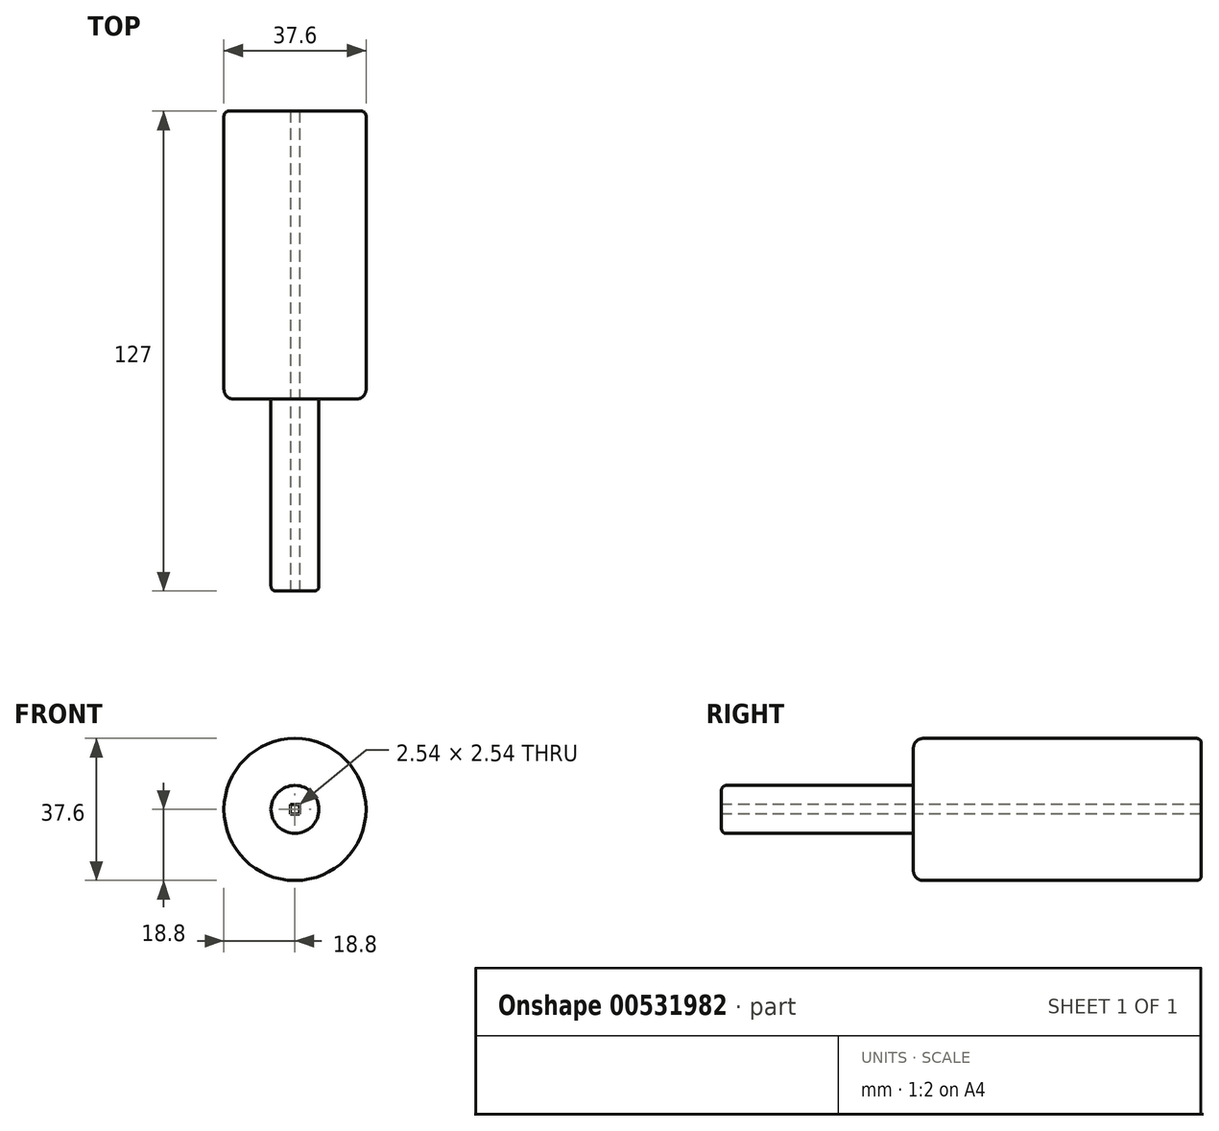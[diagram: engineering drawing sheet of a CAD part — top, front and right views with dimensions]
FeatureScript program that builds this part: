
annotation { "Feature Type Name" : "Feature", "Feature Type Description" : "" }
export const myFeature = defineFeature(function(context is Context, id is Id, definition is map)
    precondition{}
    {
        {
            var Q0;
            Q0=qCreatedBy(makeId("Front.planeOp"),FACE);
            var sketch = newSketch(context, id + "F0", { "sketchPlane" : qUnion([Q0])});
            skCircle(sketch, "E0", {"center": v(0, 0) * mm, "radius": 18.8 * mm});
            skSolve(sketch);
        }
        {
            var Q0;
            Q0=makeQuery(id+"F0.imprint","IMPRINT",FACE,{"disambiguationData":[TD([[makeQuery(id+"F0.imprint","IMPRINT",EDGE,{"derivedFrom":sQuery(id+"F0.wireOp",EDGE,"E0")}),1.0]])]});
            var sketch = newSketch(context, id + "F1", { "sketchPlane" : qUnion([Q0])});
            skCircle(sketch, "E1", {"center": v(0, 0) * mm, "radius": 6.35 * mm});
            skSolve(sketch);
        }
        {
            var Q0;
            Q0 = qSketchRegion(id + "F0", true);
            extrude(context, id + "F2", {"entities" : qUnion([Q0]), "depth" : 76.2 * mm, "offsetDistance" : 25.4 * mm});
        }
        {
            var Q0;
            Q0=makeQuery(id+"F1.imprint","IMPRINT",FACE,{"disambiguationData":[TD([[makeQuery(id+"F1.imprint","IMPRINT",EDGE,{"derivedFrom":sQuery(id+"F1.wireOp",EDGE,"E1")}),1.0]])]});
            extrude(context, id + "F3", {"entities" : qUnion([Q0]), "operationType" : NewBodyOperationType.ADD, "depth" : 127 * mm, "offsetDistance" : 25.4 * mm});
        }
        {
            var Q0;
            Q0=makeQuery(id+"F2.opExtrude","CAP_EDGE",EDGE,{"disambiguationData":[OSD([sQuery(id+"F0.wireOp",EDGE,"E0")])],"isStart":true});
            var Q1;
            Q1=makeQuery(id+"F3.opExtrude","CAP_EDGE",EDGE,{"disambiguationData":[OSD([sQuery(id+"F1.wireOp",EDGE,"E1")])],"isStart":false});
            fillet(context, id + "F4", {"entities" : qUnion([Q0, Q1]), "radius" : 1.27 * mm, "tangentPropagation" : true, "allowEdgeOverflow" : false});
        }
        {
            var Q0;
            Q0=makeQuery(id+"F3.opExtrude","CAP_FACE",FACE,{"disambiguationData":[OSD([sQuery(id+"F1.wireOp",EDGE,"E1")])],"isStart":false});
            var sketch = newSketch(context, id + "F5", { "sketchPlane" : qUnion([Q0])});
            skLineSegment(sketch, "E2.bottom", {"start": v(1.27, 1.27) * mm, "end": v(-1.27, 1.27) * mm});
            skLineSegment(sketch, "E2.top", {"start": v(1.27, -1.27) * mm, "end": v(-1.27, -1.27) * mm});
            skLineSegment(sketch, "E2.left", {"start": v(1.27, 1.27) * mm, "end": v(1.27, -1.27) * mm});
            skLineSegment(sketch, "E2.right", {"start": v(-1.27, 1.27) * mm, "end": v(-1.27, -1.27) * mm});
            skPoint(sketch, "E2.middle", {"position": v(0, 0) * mm});
            skSolve(sketch);
        }
        {
            var Q0;
            Q0 = qSketchRegion(id + "F5", true);
            extrude(context, id + "F6", {"entities" : qUnion([Q0]), "operationType" : NewBodyOperationType.REMOVE, "oppositeDirection" : true, "depth" : 127 * mm, "offsetDistance" : 25.4 * mm});
        }
        {
            var Q0;
            Q0=makeQuery(id+"F2.opExtrude","CAP_EDGE",EDGE,{"disambiguationData":[OSD([sQuery(id+"F0.wireOp",EDGE,"E0")])],"isStart":false});
            fillet(context, id + "F7", {"entities" : qUnion([Q0]), "radius" : 2.54 * mm, "tangentPropagation" : true, "allowEdgeOverflow" : false});
        }
    });
